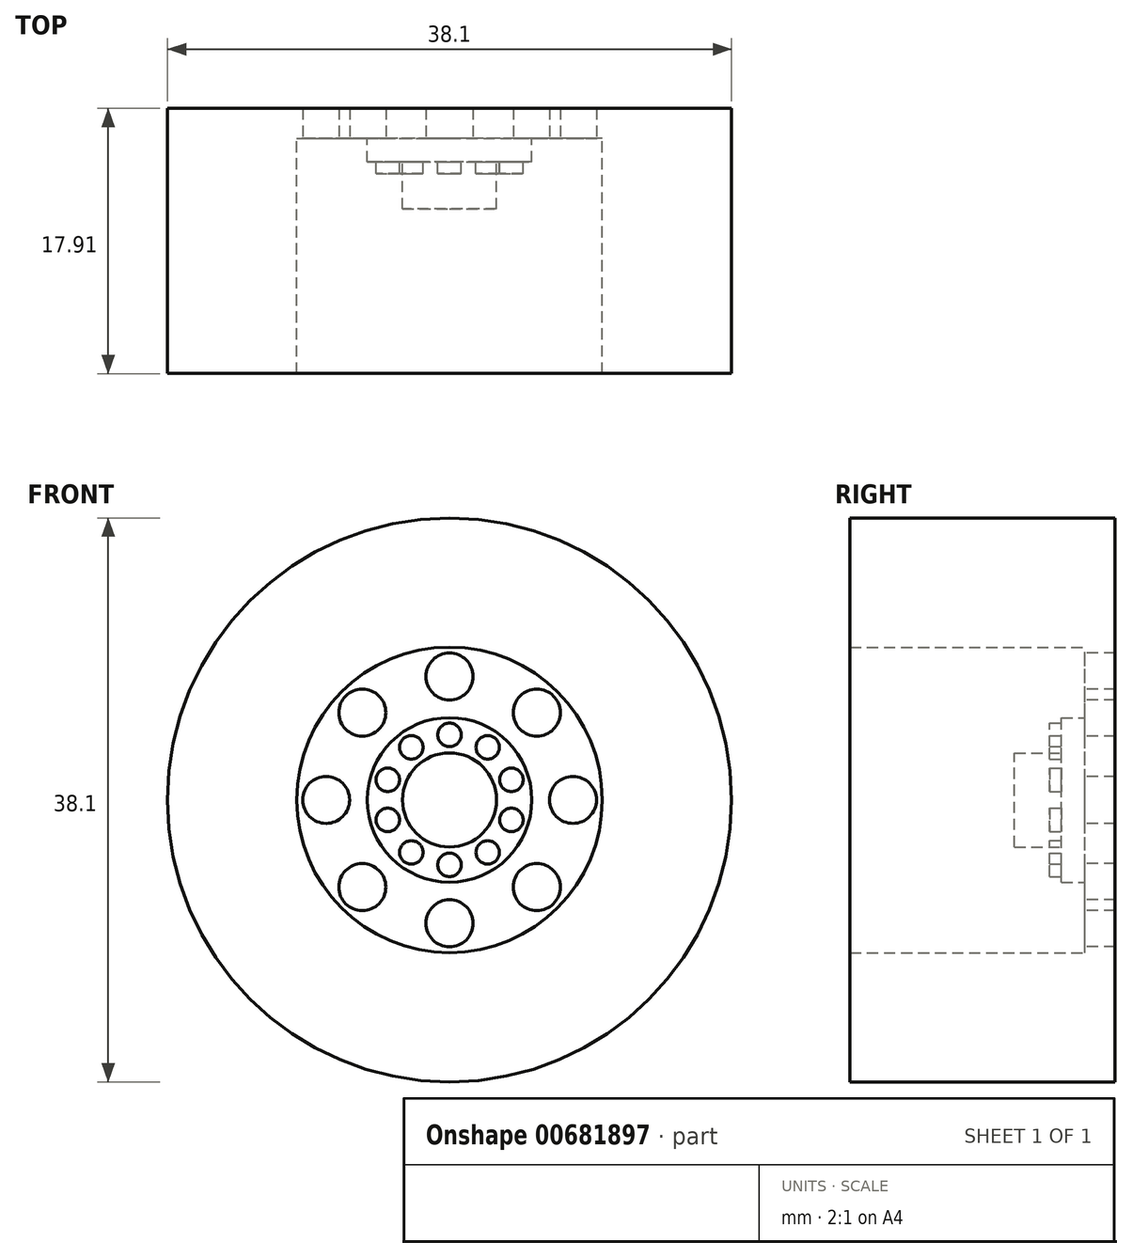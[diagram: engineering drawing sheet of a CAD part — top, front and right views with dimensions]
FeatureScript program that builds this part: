
annotation { "Feature Type Name" : "Feature", "Feature Type Description" : "" }
export const myFeature = defineFeature(function(context is Context, id is Id, definition is map)
    precondition{}
    {
        {
            var Q0;
            Q0=qCreatedBy(makeId("Front.planeOp"),FACE);
            var sketch = newSketch(context, id + "F0", { "sketchPlane" : qUnion([Q0])});
            skCircle(sketch, "E0", {"center": v(0, 0) * mm, "radius": 19.05 * mm});
            skSolve(sketch);
        }
        {
            var Q0;
            Q0=makeQuery(id+"F0.imprint","IMPRINT",FACE,{"disambiguationData":[TD([[makeQuery(id+"F0.imprint","IMPRINT",EDGE,{"derivedFrom":sQuery(id+"F0.wireOp",EDGE,"E0")}),1.0]])]});
            extrude(context, id + "F1", {"entities" : qUnion([Q0]), "depth" : 2.03 * mm, "offsetDistance" : 25.4 * mm});
        }
        {
            var Q0;
            Q0=makeQuery(id+"F1.opExtrude","CAP_FACE",FACE,{"disambiguationData":[OSD([sQuery(id+"F0.wireOp",EDGE,"E0")])],"isStart":false});
            var sketch = newSketch(context, id + "F2", { "sketchPlane" : qUnion([Q0])});
            skCircle(sketch, "E1", {"center": v(0, 8.34) * mm, "radius": 1.59 * mm});
            skCircle(sketch, "E2.1.0", {"center": v(-5.9, 5.9) * mm, "radius": 1.59 * mm});
            skCircle(sketch, "E2.2.0", {"center": v(-8.34, 0) * mm, "radius": 1.59 * mm});
            skCircle(sketch, "E2.3.0", {"center": v(-5.9, -5.9) * mm, "radius": 1.59 * mm});
            skCircle(sketch, "E2.4.0", {"center": v(0, -8.34) * mm, "radius": 1.59 * mm});
            skCircle(sketch, "E2.5.0", {"center": v(5.9, -5.9) * mm, "radius": 1.59 * mm});
            skCircle(sketch, "E2.6.0", {"center": v(8.34, 0) * mm, "radius": 1.59 * mm});
            skCircle(sketch, "E2.7.0", {"center": v(5.9, 5.9) * mm, "radius": 1.59 * mm});
            skPoint(sketch, "E2.center", {"position": v(0, 0) * mm});
            skSolve(sketch);
        }
        {
            var Q0;
            Q0=makeQuery(id+"F2.imprint","IMPRINT",FACE,{"disambiguationData":[TD([[makeQuery(id+"F2.imprint","IMPRINT",EDGE,{"derivedFrom":sQuery(id+"F2.wireOp",EDGE,"E1")}),1.0]])]});
            var Q1;
            Q1=makeQuery(id+"F2.imprint","IMPRINT",FACE,{"disambiguationData":[TD([[makeQuery(id+"F2.imprint","IMPRINT",EDGE,{"derivedFrom":sQuery(id+"F2.wireOp",EDGE,"E2.7.0")}),1.0]])]});
            var Q2;
            Q2=makeQuery(id+"F2.imprint","IMPRINT",FACE,{"disambiguationData":[TD([[makeQuery(id+"F2.imprint","IMPRINT",EDGE,{"derivedFrom":sQuery(id+"F2.wireOp",EDGE,"E2.6.0")}),1.0]])]});
            var Q3;
            Q3=makeQuery(id+"F2.imprint","IMPRINT",FACE,{"disambiguationData":[TD([[makeQuery(id+"F2.imprint","IMPRINT",EDGE,{"derivedFrom":sQuery(id+"F2.wireOp",EDGE,"E2.5.0")}),1.0]])]});
            var Q4;
            Q4=makeQuery(id+"F2.imprint","IMPRINT",FACE,{"disambiguationData":[TD([[makeQuery(id+"F2.imprint","IMPRINT",EDGE,{"derivedFrom":sQuery(id+"F2.wireOp",EDGE,"E2.3.0")}),1.0]])]});
            var Q5;
            Q5=makeQuery(id+"F2.imprint","IMPRINT",FACE,{"disambiguationData":[TD([[makeQuery(id+"F2.imprint","IMPRINT",EDGE,{"derivedFrom":sQuery(id+"F2.wireOp",EDGE,"E2.1.0")}),1.0]])]});
            var Q6;
            Q6=makeQuery(id+"F2.imprint","IMPRINT",FACE,{"disambiguationData":[TD([[makeQuery(id+"F2.imprint","IMPRINT",EDGE,{"derivedFrom":sQuery(id+"F2.wireOp",EDGE,"E2.2.0")}),1.0]])]});
            var Q7;
            Q7=makeQuery(id+"F2.imprint","IMPRINT",FACE,{"disambiguationData":[TD([[makeQuery(id+"F2.imprint","IMPRINT",EDGE,{"derivedFrom":sQuery(id+"F2.wireOp",EDGE,"E2.4.0")}),1.0]])]});
            extrude(context, id + "F3", {"entities" : qUnion([Q0, Q1, Q2, Q3, Q4, Q5, Q6, Q7]), "operationType" : NewBodyOperationType.REMOVE, "oppositeDirection" : true, "depth" : 20.32 * mm, "offsetDistance" : 25.4 * mm});
        }
        {
            var Q0;
            Q0=makeQuery(id+"F1.opExtrude","CAP_FACE",FACE,{"disambiguationData":[OSD([sQuery(id+"F0.wireOp",EDGE,"E0")])],"isStart":false});
            var sketch = newSketch(context, id + "F4", { "sketchPlane" : qUnion([Q0])});
            skCircle(sketch, "E3", {"center": v(0, 0) * mm, "radius": 5.56 * mm});
            skSolve(sketch);
        }
        {
            var Q0;
            Q0=makeQuery(id+"F4.imprint","IMPRINT",FACE,{"disambiguationData":[TD([[makeQuery(id+"F4.imprint","IMPRINT",EDGE,{"derivedFrom":sQuery(id+"F4.wireOp",EDGE,"E3")}),1.0]])]});
            extrude(context, id + "F5", {"entities" : qUnion([Q0]), "operationType" : NewBodyOperationType.ADD, "depth" : 1.59 * mm, "offsetDistance" : 25.4 * mm});
        }
        {
            var Q0;
            Q0=makeQuery(id+"F5.opExtrude","CAP_FACE",FACE,{"disambiguationData":[OSD([sQuery(id+"F4.wireOp",EDGE,"E3")])],"isStart":false});
            var sketch = newSketch(context, id + "F6", { "sketchPlane" : qUnion([Q0])});
            skCircle(sketch, "E4", {"center": v(0, 0) * mm, "radius": 3.18 * mm});
            skSolve(sketch);
        }
        {
            var Q0;
            Q0=makeQuery(id+"F6.imprint","IMPRINT",FACE,{"disambiguationData":[TD([[makeQuery(id+"F6.imprint","IMPRINT",EDGE,{"derivedFrom":sQuery(id+"F6.wireOp",EDGE,"E4")}),1.0]])]});
            extrude(context, id + "F7", {"entities" : qUnion([Q0]), "operationType" : NewBodyOperationType.ADD, "depth" : 3.17 * mm, "offsetDistance" : 25.4 * mm});
        }
        {
            var Q0;
            Q0=makeQuery(id+"F5.opExtrude","CAP_FACE",FACE,{"disambiguationData":[OSD([sQuery(id+"F4.wireOp",EDGE,"E3")])],"isStart":false});
            var sketch = newSketch(context, id + "F8", { "sketchPlane" : qUnion([Q0])});
            skCircle(sketch, "E5", {"center": v(0, 4.39) * mm, "radius": 0.8 * mm});
            skCircle(sketch, "E6.1.0", {"center": v(-2.58, 3.55) * mm, "radius": 0.8 * mm});
            skCircle(sketch, "E6.2.0", {"center": v(-4.17, 1.36) * mm, "radius": 0.8 * mm});
            skCircle(sketch, "E6.3.0", {"center": v(-4.17, -1.36) * mm, "radius": 0.8 * mm});
            skCircle(sketch, "E6.4.0", {"center": v(-2.58, -3.55) * mm, "radius": 0.8 * mm});
            skCircle(sketch, "E6.5.0", {"center": v(0, -4.39) * mm, "radius": 0.8 * mm});
            skCircle(sketch, "E6.6.0", {"center": v(2.58, -3.55) * mm, "radius": 0.8 * mm});
            skCircle(sketch, "E6.7.0", {"center": v(4.17, -1.36) * mm, "radius": 0.8 * mm});
            skCircle(sketch, "E6.8.0", {"center": v(4.17, 1.36) * mm, "radius": 0.8 * mm});
            skCircle(sketch, "E6.9.0", {"center": v(2.58, 3.55) * mm, "radius": 0.8 * mm});
            skPoint(sketch, "E6.center", {"position": v(0, 0) * mm});
            skSolve(sketch);
        }
        {
            var Q0;
            Q0=makeQuery(id+"F8.imprint","IMPRINT",FACE,{"disambiguationData":[TD([[makeQuery(id+"F8.imprint","IMPRINT",EDGE,{"derivedFrom":sQuery(id+"F8.wireOp",EDGE,"E5")}),1.0]])]});
            var Q1;
            Q1=makeQuery(id+"F8.imprint","IMPRINT",FACE,{"disambiguationData":[TD([[makeQuery(id+"F8.imprint","IMPRINT",EDGE,{"derivedFrom":sQuery(id+"F8.wireOp",EDGE,"E6.9.0")}),1.0]])]});
            var Q2;
            Q2=makeQuery(id+"F8.imprint","IMPRINT",FACE,{"disambiguationData":[TD([[makeQuery(id+"F8.imprint","IMPRINT",EDGE,{"derivedFrom":sQuery(id+"F8.wireOp",EDGE,"E6.8.0")}),1.0]])]});
            var Q3;
            Q3=makeQuery(id+"F8.imprint","IMPRINT",FACE,{"disambiguationData":[TD([[makeQuery(id+"F8.imprint","IMPRINT",EDGE,{"derivedFrom":sQuery(id+"F8.wireOp",EDGE,"E6.6.0")}),1.0]])]});
            var Q4;
            Q4=makeQuery(id+"F8.imprint","IMPRINT",FACE,{"disambiguationData":[TD([[makeQuery(id+"F8.imprint","IMPRINT",EDGE,{"derivedFrom":sQuery(id+"F8.wireOp",EDGE,"E6.7.0")}),1.0]])]});
            var Q5;
            Q5=makeQuery(id+"F8.imprint","IMPRINT",FACE,{"disambiguationData":[TD([[makeQuery(id+"F8.imprint","IMPRINT",EDGE,{"derivedFrom":sQuery(id+"F8.wireOp",EDGE,"E6.5.0")}),1.0]])]});
            var Q6;
            Q6=makeQuery(id+"F8.imprint","IMPRINT",FACE,{"disambiguationData":[TD([[makeQuery(id+"F8.imprint","IMPRINT",EDGE,{"derivedFrom":sQuery(id+"F8.wireOp",EDGE,"E6.4.0")}),1.0]])]});
            var Q7;
            Q7=makeQuery(id+"F8.imprint","IMPRINT",FACE,{"disambiguationData":[TD([[makeQuery(id+"F8.imprint","IMPRINT",EDGE,{"derivedFrom":sQuery(id+"F8.wireOp",EDGE,"E6.3.0")}),1.0]])]});
            var Q8;
            Q8=makeQuery(id+"F8.imprint","IMPRINT",FACE,{"disambiguationData":[TD([[makeQuery(id+"F8.imprint","IMPRINT",EDGE,{"derivedFrom":sQuery(id+"F8.wireOp",EDGE,"E6.2.0")}),1.0]])]});
            var Q9;
            Q9=makeQuery(id+"F8.imprint","IMPRINT",FACE,{"disambiguationData":[TD([[makeQuery(id+"F8.imprint","IMPRINT",EDGE,{"derivedFrom":sQuery(id+"F8.wireOp",EDGE,"E6.1.0")}),1.0]])]});
            extrude(context, id + "F9", {"entities" : qUnion([Q0, Q1, Q2, Q3, Q4, Q5, Q6, Q7, Q8, Q9]), "operationType" : NewBodyOperationType.ADD, "depth" : 0.8 * mm, "offsetDistance" : 25.4 * mm});
        }
        {
            var Q0;
            Q0=makeQuery(id+"F0.imprint","IMPRINT",FACE,{"disambiguationData":[TD([[makeQuery(id+"F0.imprint","IMPRINT",EDGE,{"derivedFrom":sQuery(id+"F0.wireOp",EDGE,"E0")}),1.0]])]});
            var sketch = newSketch(context, id + "F10", { "sketchPlane" : qUnion([Q0])});
            skCircle(sketch, "E7", {"center": v(0, 0) * mm, "radius": 3.17 * mm});
            skSolve(sketch);
        }
        {
            var Q0;
            Q0=sQuery(id+"F10.wireOp",EDGE,"E7");
            extrude(context, id + "F11", {"bodyType" : ToolBodyType.SURFACE, "surfaceEntities" : qUnion([Q0]), "oppositeDirection" : true, "depth" : 9.52 * mm, "offsetDistance" : 25.4 * mm});
        }
        {
            var Q0;
            Q0=makeQuery(id+"F1.opExtrude","CAP_FACE",FACE,{"disambiguationData":[OSD([sQuery(id+"F0.wireOp",EDGE,"E0")])],"isStart":false});
            var sketch = newSketch(context, id + "F12", { "sketchPlane" : qUnion([Q0])});
            skCircle(sketch, "E8", {"center": v(0, 0) * mm, "radius": 10.32 * mm});
            skSolve(sketch);
        }
        {
            var Q0;
            Q0=makeQuery(id+"F12.imprint","IMPRINT",FACE,{"disambiguationData":[TD([[makeQuery(id+"F12.imprint","IMPRINT",EDGE,{"derivedFrom":sQuery(id+"F12.wireOp",EDGE,"E8")}),-1.0]])]});
            extrude(context, id + "F13", {"entities" : qUnion([Q0]), "operationType" : NewBodyOperationType.ADD, "depth" : 1.59 * mm, "offsetDistance" : 25.4 * mm});
        }
        {
            var Q0;
            Q0=makeQuery(id+"F13.opExtrude","CAP_FACE",FACE,{"disambiguationData":[OSD([sQuery(id+"F0.wireOp",EDGE,"E0"),sQuery(id+"F12.wireOp",EDGE,"E8")])],"isStart":false});
            extrude(context, id + "F14", {"entities" : qUnion([Q0]), "operationType" : NewBodyOperationType.ADD, "depth" : 14.29 * mm, "offsetDistance" : 25.4 * mm});
        }
    });
